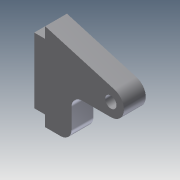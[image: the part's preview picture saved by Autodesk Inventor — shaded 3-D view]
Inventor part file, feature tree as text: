
AUTODESK INVENTOR PART (.ipt)
format: ipt  version: 2011 (Build 150239000, 239)  size: 94,208 bytes
history: native  units: in
note: dims shown in document units (in); Inventor stores cm internally (conversion verified against a paired STEP export)
features: extrude x1, fillet x1, sketch x1
ambient origin geometry x8: Origin, YZ Plane, XZ Plane, XY Plane, X Axis, Y Axis, Z Axis, Center Point
bodies: Solid1 (feature_tree)
feature tree (3):
  extrude  "Extrusion1"  Depth=1.5in
  fillet  "Fillet1"  Radius=0.25in
  sketch  "Sketch1"  dims[d0=0.25in d1=1.5in d2=0.25in d3=0.25in d4=0.5in d5=1.504in d6=0.2598in d7=0.3in d8=0.9in d9=0.5in d10=0.0in d11=0.25in]
